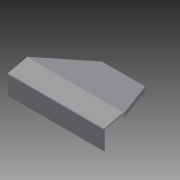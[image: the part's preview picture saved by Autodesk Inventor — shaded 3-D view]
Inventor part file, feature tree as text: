
AUTODESK INVENTOR PART (.ipt)
format: ipt  version: 2014 SP2 (Build 180246200, 246)  size: 252,928 bytes
history: native  units: mm
features: sketch x7, other x5, extrude x2
ambient origin geometry x8: Origin, YZ Plane, XZ Plane, XY Plane, X Axis, Y Axis, Z Axis, Center Point
bodies: Solid1 (feature_tree)
feature tree (14):
  extrude  "Extrusion1"  Depth=542.0mm
  other  "Bend Part1"
  other  "Bend Part2"
  other  "Bend Part3"
  other  "Bend Part4"
  other  "Bend Part5"
  extrude  "Extrusion2"  Depth=4.0mm
  sketch  "Sketch1"  dims[d0=594.0mm d1=542.0mm]
  sketch  "Sketch2"  dims[d2=4.0mm d3=0.0mm d4=167.0mm d5=308.0mm]
  sketch  "Sketch3"  dims[d6=308.0mm d7=167.0mm d8=260.0mm]
  sketch  "Sketch4"  dims[d9=56.0mm]
  sketch  "Sketch5"  dims[d10=74.0mm]
  sketch  "Sketch6"  dims[d11=74.0mm]
  sketch  "Sketch8"  dims[d12=4.0mm d13=14.3117mm d14=1.0mm d15=4.0mm d16=90.0deg d17=1.0mm d18=1.0mm d20=4.0mm d21=14.3117mm d23=1.0mm d24=4.0mm d25=30.0deg d26=153.0mm d27=152.0mm d28=800.0mm d29=400.0mm d30=0.0mm d31=0.0mm d33=18.0mm d34=18.0mm d35=78.0mm d38=113.0mm d39=4.0mm d40=13.439035mm d41=234.0mm d42=20.0mm d43=20.0mm d44=90.0deg d45=90.0deg d46=90.0deg d47=90.0deg]
